# Revit family: Loading-Dock-Equipment_Leveler_McGuire_Hydraulic-HP
name_source: partatom
category: Specialty Equipment
units: mm (PartAtom-declared; Revit-internal decimal feet)

## family parameters
Classification Number = 23.50.70.14.11
Cut with Voids When Loaded = No
Enable Cutting in Views = No
Host = Face
Maintain Annotation Orientation = No
Part Type = Normal
Room Calculation Point = No
Round Connector Dimension = Use Radius
Shared = No

## types (1)
- Loading-Dock-Equipment_Leveler_McGuire_Hydraulic-HP
    Assembly Code = E1030300
    Capacity = as Specified
    Conduit Entry Depth = 1' - 2"
    Conduit Entry_Primary Side Offset = 0' - 10"
    Default Elevation = 0' - 0"
    Description = McGuire Loading Dock Product as Specified
    Expected Lifespan (Years) = 0
    Green Building-LEED = http://www.arcat.com
    Keynote = 11600
    Lip Inset = 0' - 0"
    Maintenance Schedule (Months) = 0
    Manufacturer = McGuire
    Manufacturer Fax = 262-255-4199
    Manufacturer Website = http://www.wbmcguire.com
    Model = As Specified
    Pit Depth = 1' - 8"
    Pit Length = 7' - 0"
    Pit Width = 7' - 1"
    Product Data = http://www.arcat.com
    Revision = R1_2017-01
    Sales Information = http://www.wbmcguire.com
    URL = http://www.wbmcguire.com
    Unit Width = 6' - 11"
    Warranty Duration (Years) = 0

## geometry (parser evidence)
native form markers: Blend x2, Sweep x2
no freeform markers — native parametric forms only
